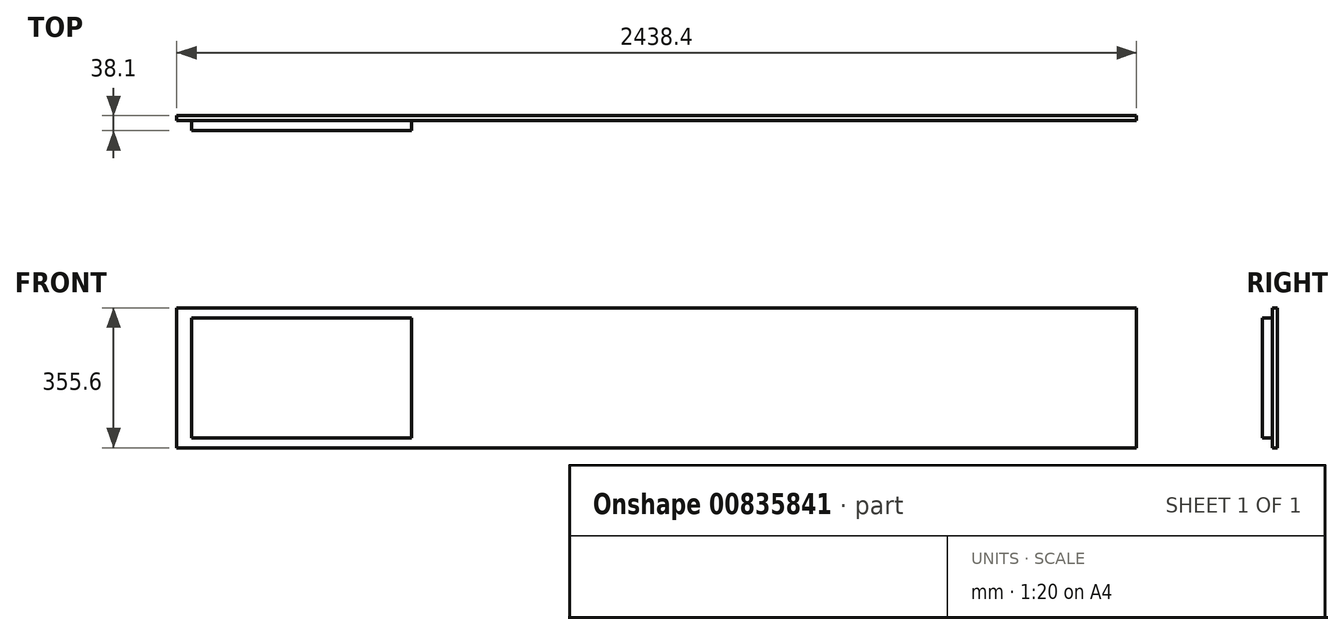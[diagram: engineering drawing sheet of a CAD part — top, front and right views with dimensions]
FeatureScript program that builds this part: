
annotation { "Feature Type Name" : "Feature", "Feature Type Description" : "" }
export const myFeature = defineFeature(function(context is Context, id is Id, definition is map)
    precondition{}
    {
        {
            var Q0;
            Q0=qCreatedBy(makeId("Front.planeOp"),FACE);
            var sketch = newSketch(context, id + "F0", { "sketchPlane" : qUnion([Q0])});
            skLineSegment(sketch, "E0.bottom", {"start": v(0, 0) * mm, "end": v(2438.4, 0) * mm});
            skLineSegment(sketch, "E0.top", {"start": v(0, 355.6) * mm, "end": v(2438.4, 355.6) * mm});
            skLineSegment(sketch, "E0.left", {"start": v(0, 0) * mm, "end": v(0, 355.6) * mm});
            skLineSegment(sketch, "E0.right", {"start": v(2438.4, 0) * mm, "end": v(2438.4, 355.6) * mm});
            skSolve(sketch);
        }
        {
            var Q0;
            Q0 = qSketchRegion(id + "F0", true);
            extrude(context, id + "F1", {"entities" : qUnion([Q0]), "depth" : 12.7 * mm, "offsetDistance" : 25.4 * mm});
        }
        {
            var Q0;
            Q0=makeQuery(id+"F1.opExtrude","CAP_FACE",FACE,{"disambiguationData":[OSD([sQuery(id+"F0.wireOp",EDGE,"E0.bottom"),sQuery(id+"F0.wireOp",EDGE,"E0.top"),sQuery(id+"F0.wireOp",EDGE,"E0.left"),sQuery(id+"F0.wireOp",EDGE,"E0.right")])],"isStart":false});
            var sketch = newSketch(context, id + "F2", { "sketchPlane" : qUnion([Q0])});
            skLineSegment(sketch, "E1.bottom", {"start": v(38.1, 330.2) * mm, "end": v(596.9, 330.2) * mm});
            skLineSegment(sketch, "E1.top", {"start": v(38.1, 25.4) * mm, "end": v(596.9, 25.4) * mm});
            skLineSegment(sketch, "E1.left", {"start": v(38.1, 330.2) * mm, "end": v(38.1, 25.4) * mm});
            skLineSegment(sketch, "E1.right", {"start": v(596.9, 330.2) * mm, "end": v(596.9, 25.4) * mm});
            skSolve(sketch);
        }
        {
            var Q0;
            Q0 = qSketchRegion(id + "F2", true);
            extrude(context, id + "F3", {"entities" : qUnion([Q0]), "depth" : 25.4 * mm, "offsetDistance" : 25.4 * mm});
        }
    });
